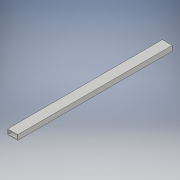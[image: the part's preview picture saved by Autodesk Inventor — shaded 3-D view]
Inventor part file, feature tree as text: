
AUTODESK INVENTOR PART (.ipt)
format: ipt  version: 2018 (Build 220112000, 112)  size: 97,792 bytes
history: native  units: in
note: dims shown in document units (in); Inventor stores cm internally (conversion verified against a paired STEP export)
features: extrude x1, sketch x1
ambient origin geometry x8: Origin, YZ Plane, XZ Plane, XY Plane, X Axis, Y Axis, Z Axis, Center Point
bodies: Solid1 (feature_tree)
feature tree (2):
  extrude  "Extrusion1"  Depth=1.0in
  sketch  "Sketch1"  dims[d0=2.0in d1=1.0in d2=0.125in d3=30.87in d4=0.0in]
